# Revit family: Worksurface-Teknion-JNWPSN-Peninsula-R2018
name_source: partatom
category: Furniture
revit_build: Autodesk Revit 2018 (Build: 20190510_1515(x64)
units: mm (PartAtom-declared; Revit-internal decimal feet)

## family parameters
Always vertical = Yes
Cut with Voids When Loaded = No
OmniClass Number = 23.40.20.00
OmniClass Title = General Furniture and Specialties
Room Calculation Point = No
Shared = Yes
Work Plane-Based = No

## types (6) — shared parameters
Assembly Code = E2020200
Manufacturer = Teknion
Manufacturer Fax = 416.661.4586
Part Number = JNWPSN
Product Documentation Link = https://www.teknion.com
Product Line = Expansion Cityline
Product Page URL = https://www.teknion.com
Series = Expansion Cityline
Sustainability Data = https://www.teknion.com
URL = www.teknion.com
Unit Weight URL = http://www.teknion.com
Warranty = http://www.teknion.com

## per-type parameters (varying)
| type | Corner | Depth | Description | Model | Standard | Worksurface Edge |
| 24" Depth, Curved Corner Detail | Yes | 24 " | Peninsula Worksurface, 24" Depth, Curved Corner Detail | JNWPSN24_C_ | No | 5 " |
| 24" Depth, Standard Corner Detail | No | 24 " | Peninsula Worksurface, 24" Depth, Standard Corner Detail | JNWPSN24_S_ | Yes | 1 " |
| 30" Depth, Curved Corner Detail | Yes | 30 " | Peninsula Worksurface, 30" Depth, Curved Corner Detail | JNWPSN30_C_ | No | 5 " |
| 30" Depth, Standard Corner Detail | No | 30 " | Peninsula Worksurface, 30" Depth, Standard Corner Detail | JNWPSN30_S_ | Yes | 1 " |
| 36" Depth, Curved Corner Detail | Yes | 36 " | Peninsula Worksurface, 36" Depth, Curved Corner Detail | JNWPSN36_C_ | No | 5 " |
| 36" Depth, Standard Corner Detail | No | 36 " | Peninsula Worksurface, 36" Depth, Standard Corner Detail | JNWPSN36_S_ | Yes | 1 " |

## geometry (parser evidence)
native form markers: Sweep x2
no freeform markers — native parametric forms only
